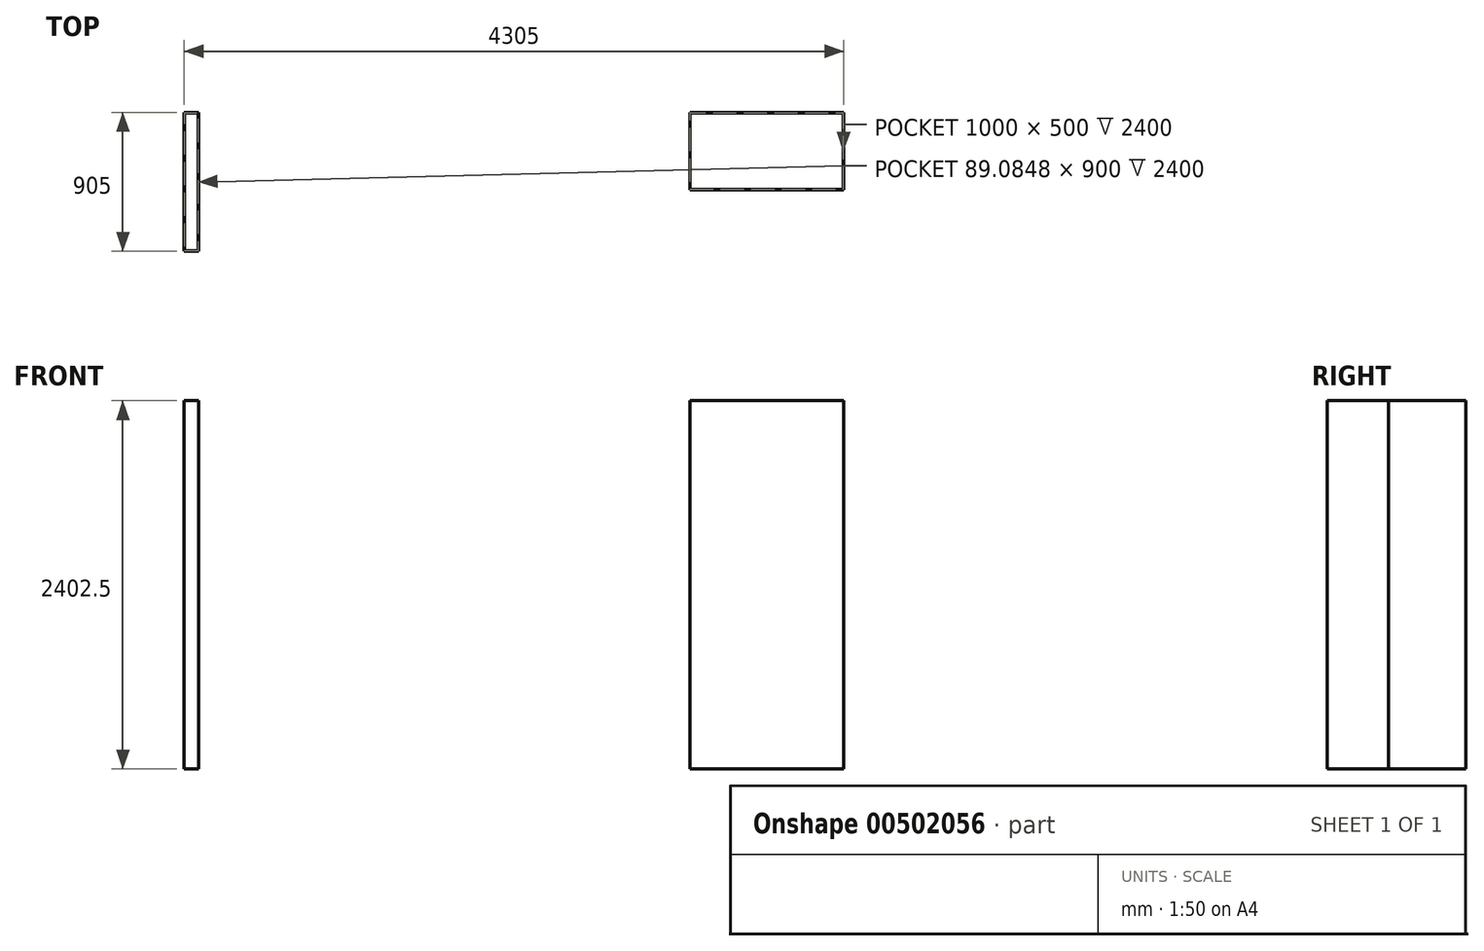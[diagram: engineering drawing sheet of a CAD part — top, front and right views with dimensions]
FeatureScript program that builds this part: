
annotation { "Feature Type Name" : "Feature", "Feature Type Description" : "" }
export const myFeature = defineFeature(function(context is Context, id is Id, definition is map)
    precondition{}
    {
        {
            var Q0;
            Q0=qCreatedBy(makeId("Top.planeOp"),FACE);
            var sketch = newSketch(context, id + "F0", { "sketchPlane" : qUnion([Q0])});
            skLineSegment(sketch, "E0.bottom", {"start": v(-2150, 1500) * mm, "end": v(2150, 1500) * mm});
            skLineSegment(sketch, "E0.top", {"start": v(-2150, -1500) * mm, "end": v(2150, -1500) * mm});
            skLineSegment(sketch, "E0.left", {"start": v(-2150, 1500) * mm, "end": v(-2150, -1500) * mm});
            skLineSegment(sketch, "E0.right", {"start": v(2150, 1500) * mm, "end": v(2150, -1500) * mm});
            skLineSegment(sketch, "E1.bottom", {"start": v(2029.55, 1500) * mm, "end": v(2713.76, 1500) * mm});
            skLineSegment(sketch, "E1.top", {"start": v(2029.55, 0) * mm, "end": v(2713.76, 0) * mm});
            skLineSegment(sketch, "E1.left", {"start": v(2029.55, 1500) * mm, "end": v(2029.55, 0) * mm});
            skLineSegment(sketch, "E1.right", {"start": v(2713.76, 1500) * mm, "end": v(2713.76, 0) * mm});
            skLineSegment(sketch, "E2.bottom", {"start": v(-2060.92, 1500) * mm, "end": v(-2749.4, 1500) * mm});
            skLineSegment(sketch, "E2.top", {"start": v(-2060.92, 600) * mm, "end": v(-2749.4, 600) * mm});
            skLineSegment(sketch, "E2.left", {"start": v(-2060.92, 1500) * mm, "end": v(-2060.92, 600) * mm});
            skLineSegment(sketch, "E2.right", {"start": v(-2749.4, 1500) * mm, "end": v(-2749.4, 600) * mm});
            skLineSegment(sketch, "E3.bottom", {"start": v(-1150, -1500) * mm, "end": v(510, -1500) * mm});
            skLineSegment(sketch, "E3.top", {"start": v(-1150, 840) * mm, "end": v(510, 840) * mm});
            skLineSegment(sketch, "E3.left", {"start": v(-1150, -1500) * mm, "end": v(-1150, 840) * mm});
            skLineSegment(sketch, "E3.right", {"start": v(510, -1500) * mm, "end": v(510, 840) * mm});
            skLineSegment(sketch, "E4.bottom", {"start": v(1150, 1500) * mm, "end": v(2150, 1500) * mm});
            skLineSegment(sketch, "E4.top", {"start": v(1150, 1000) * mm, "end": v(2150, 1000) * mm});
            skLineSegment(sketch, "E4.left", {"start": v(1150, 1500) * mm, "end": v(1150, 1000) * mm});
            skLineSegment(sketch, "E4.right", {"start": v(2150, 1500) * mm, "end": v(2150, 1000) * mm});
            skLineSegment(sketch, "E5.bottom", {"start": v(-2150, -1500) * mm, "end": v(-1550, -1500) * mm});
            skLineSegment(sketch, "E5.top", {"start": v(-2150, 0) * mm, "end": v(-1550, 0) * mm});
            skLineSegment(sketch, "E5.left", {"start": v(-2150, -1500) * mm, "end": v(-2150, 0) * mm});
            skLineSegment(sketch, "E5.right", {"start": v(-1550, -1500) * mm, "end": v(-1550, 0) * mm});
            skSolve(sketch);
        }
        {
            var Q0;
            Q0=makeQuery(id+"F0.imprint","IMPRINT",FACE,{"disambiguationData":[TD([[makeQuery(id+"F0.imprint","IMPRINT",EDGE,{"derivedFrom":sQuery(id+"F0.wireOp",EDGE,"E0.bottom")}),-1.0]])]});
            extrude(context, id + "F1", {"entities" : qUnion([Q0]), "depth" : 2400 * mm});
        }
        {
            var Q0;
            Q0=makeQuery(id+"F1.opExtrude","CAP_FACE",FACE,{"disambiguationData":[OSD([sQuery(id+"F0.wireOp",EDGE,"E0.bottom"),sQuery(id+"F0.wireOp",EDGE,"E0.top"),sQuery(id+"F0.wireOp",EDGE,"E0.left"),sQuery(id+"F0.wireOp",EDGE,"E0.right")])],"isStart":false});
            shell(context, id + "F2", {"entities" : qUnion([Q0]), "thickness" : 2.5 * mm, "oppositeDirection" : true});
        }
    });
